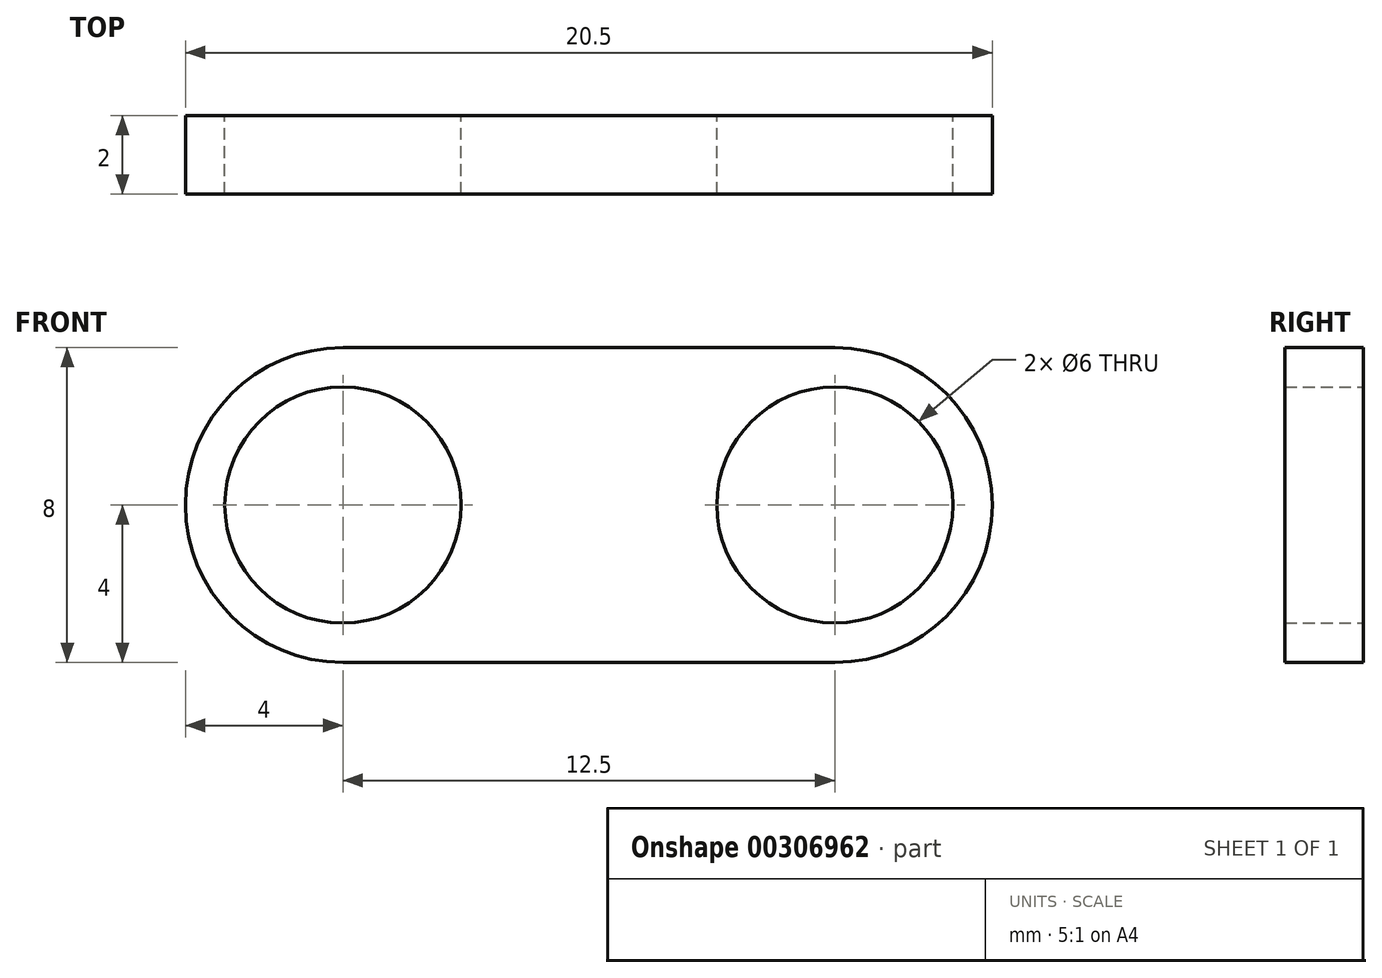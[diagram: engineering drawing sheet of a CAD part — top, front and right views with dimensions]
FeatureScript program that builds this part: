
annotation { "Feature Type Name" : "Feature", "Feature Type Description" : "" }
export const myFeature = defineFeature(function(context is Context, id is Id, definition is map)
    precondition{}
    {
        {
            var Q0;
            Q0=qCreatedBy(makeId("Front.planeOp"),FACE);
            var sketch = newSketch(context, id + "F0", { "sketchPlane" : qUnion([Q0])});
            skCircle(sketch, "E0", {"center": v(-6.25, 0) * mm, "radius": 3 * mm});
            skCircle(sketch, "E1", {"center": v(6.25, 0) * mm, "radius": 3 * mm});
            skArc(sketch, "E2", {"start": v(-6.25, 4) * mm, "mid": v(-10.25, 0) * mm, "end": v(-6.25, -4) * mm});
            skArc(sketch, "E3", {"start": v(6.25, -4) * mm, "mid": v(10.25, 0) * mm, "end": v(6.25, 4) * mm});
            skLineSegment(sketch, "E4", {"start": v(-6.25, 4) * mm, "end": v(6.25, 4) * mm});
            skLineSegment(sketch, "E5", {"start": v(-6.25, -4) * mm, "end": v(6.25, -4) * mm});
            skSolve(sketch);
        }
        {
            var Q0;
            Q0 = qSketchRegion(id + "F0", true);
            extrude(context, id + "F1", {"entities" : qUnion([Q0]), "depth" : 2 * mm});
        }
    });
